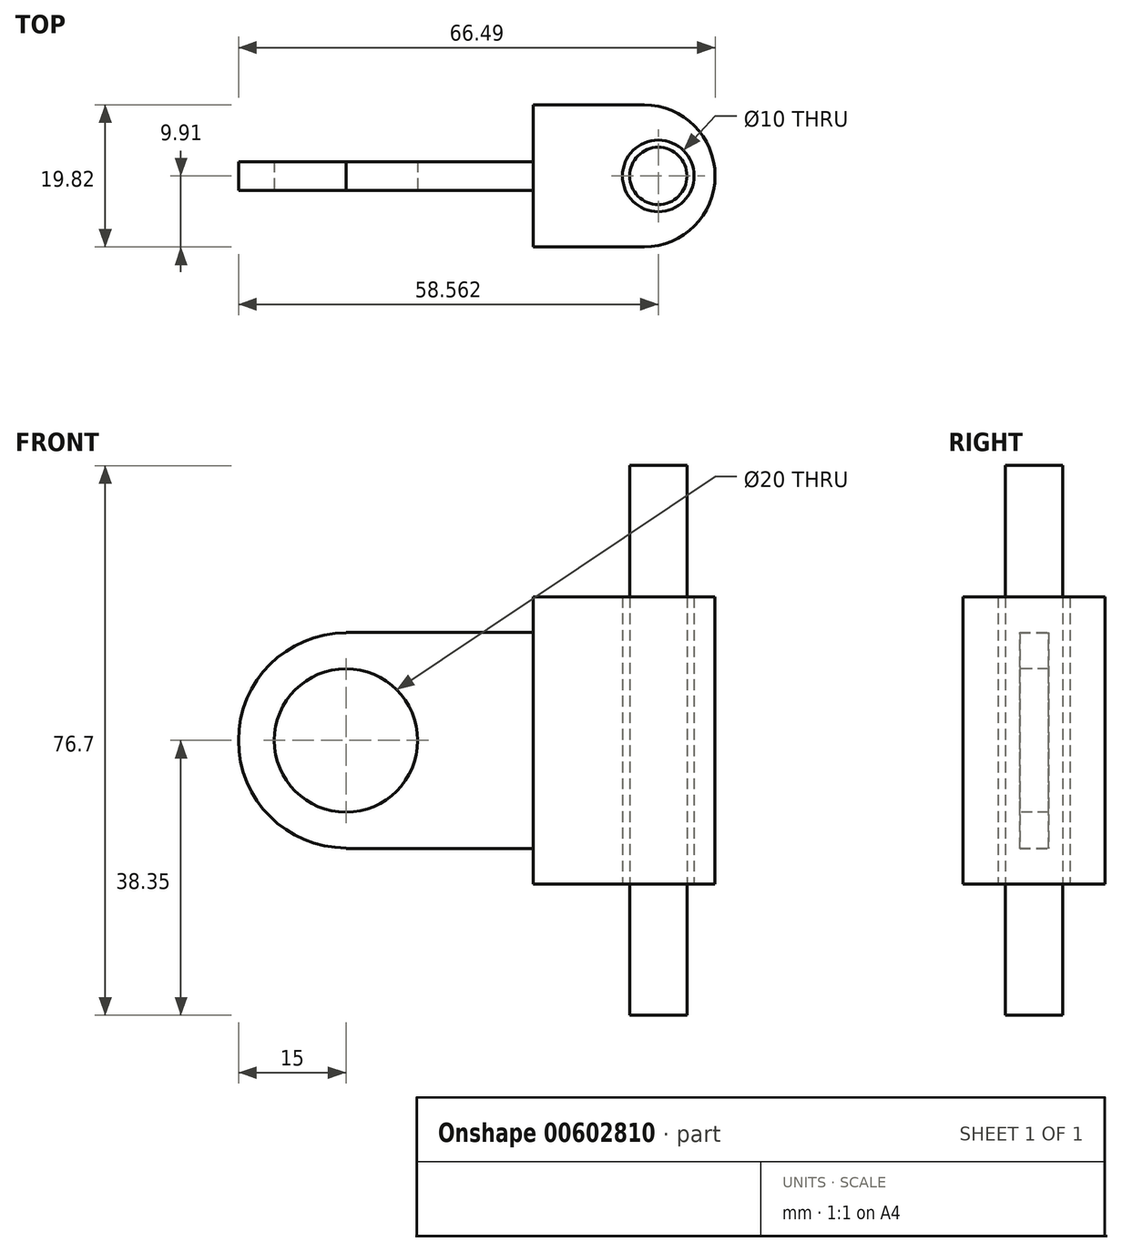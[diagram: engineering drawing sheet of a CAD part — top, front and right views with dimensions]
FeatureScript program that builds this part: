
annotation { "Feature Type Name" : "Feature", "Feature Type Description" : "" }
export const myFeature = defineFeature(function(context is Context, id is Id, definition is map)
    precondition{}
    {
        {
            var Q0;
            Q0=qCreatedBy(makeId("Front.planeOp"),FACE);
            var sketch = newSketch(context, id + "F0", { "sketchPlane" : qUnion([Q0])});
            skCircle(sketch, "E0", {"center": v(0, 0) * mm, "radius": 15 * mm});
            skSolve(sketch);
        }
        {
            var Q0;
            Q0=makeQuery(id+"F0.imprint","IMPRINT",FACE,{"disambiguationData":[TD([[makeQuery(id+"F0.imprint","IMPRINT",EDGE,{"derivedFrom":sQuery(id+"F0.wireOp",EDGE,"E0")}),1.0]])]});
            extrude(context, id + "F1", {"entities" : qUnion([Q0]), "endBound" : BoundingType.SYMMETRIC, "depth" : 4 * mm, "offsetDistance" : 25.4 * mm});
        }
        {
            var Q0;
            Q0=makeQuery(id+"F1.opExtrude","CAP_FACE",FACE,{"disambiguationData":[OSD([sQuery(id+"F0.wireOp",EDGE,"E0")])],"isStart":false});
            var sketch = newSketch(context, id + "F2", { "sketchPlane" : qUnion([Q0])});
            skPoint(sketch, "E1", {"position": v(0, 0) * mm});
            skSolve(sketch);
        }
        {
            var Q0;
            Q0=qCreatedBy(makeId("Front.planeOp"),FACE);
            var sketch = newSketch(context, id + "F3", { "sketchPlane" : qUnion([Q0])});
            skLineSegment(sketch, "E2.bottom", {"start": v(0, 0) * mm, "end": v(26.09, 0) * mm});
            skLineSegment(sketch, "E2.top", {"start": v(0, 15.07) * mm, "end": v(26.09, 15.07) * mm});
            skLineSegment(sketch, "E2.left", {"start": v(0, 0) * mm, "end": v(0, 15.07) * mm});
            skLineSegment(sketch, "E2.right", {"start": v(26.09, 0) * mm, "end": v(26.09, 15.07) * mm});
            skSolve(sketch);
        }
        {
            var Q0;
            Q0=makeQuery(id+"F3.imprint","IMPRINT",FACE,{"disambiguationData":[TD([[makeQuery(id+"F3.imprint","IMPRINT",EDGE,{"derivedFrom":sQuery(id+"F3.wireOp",EDGE,"E2.bottom")}),1.0]])]});
            extrude(context, id + "F4", {"entities" : qUnion([Q0]), "operationType" : NewBodyOperationType.ADD, "endBound" : BoundingType.SYMMETRIC, "depth" : 4 * mm, "offsetDistance" : 25.4 * mm});
        }
        {
            var Q0;
            Q0=makeQuery(id+"F1.opExtrude","SWEPT_BODY",BODY,{"disambiguationData":[OSD([sQuery(id+"F0.wireOp",EDGE,"E0")])]});
            var Q1;
            Q1=qCreatedBy(makeId("Top.planeOp"),FACE);
            mirror(context, id + "F5", {"operationType" : NewBodyOperationType.ADD, "entities" : qUnion([Q0]), "mirrorPlane" : qUnion([Q1])});
        }
        {
            var Q0;
            Q0=sQuery(id+"F2.wireOp",VERTEX,"E1");
            var Q1;
            Q1=makeQuery(id+"F1.opExtrude","SWEPT_BODY",BODY,{"disambiguationData":[OSD([sQuery(id+"F0.wireOp",EDGE,"E0")])]});
            hole(context, id + "F6", {"style" : HoleStyle.SIMPLE, "endStyle" : HoleEndStyle.THROUGH, "holeDiameter" : 20 * mm, "majorDiameter" : 6.35 * mm, "isTappedThrough" : true, "tappedDepth" : 12.7 * mm, "tapClearance" : 3, "locations" : qUnion([Q0]), "scope" : qUnion([Q1])});
        }
        {
            var Q0;
            {var subQ0=makeQuery(id+"F4.opExtrude","SWEPT_FACE",FACE,{"disambiguationData":[OSD([sQuery(id+"F3.wireOp",EDGE,"E2.right")])]});Q0=makeQuery(id+"F5.boolean.opBoolean","MERGE",FACE,{"derivedFrom":[subQ0,makeQuery(id+"F5.opPattern","COPY",FACE,{"derivedFrom":subQ0,"instanceName":"1"})]});}
            var sketch = newSketch(context, id + "F7", { "sketchPlane" : qUnion([Q0])});
            skLineSegment(sketch, "E3.bottom", {"start": v(9.9, -20.02) * mm, "end": v(-9.9, -20.02) * mm});
            skLineSegment(sketch, "E3.top", {"start": v(9.9, 20.02) * mm, "end": v(-9.9, 20.02) * mm});
            skLineSegment(sketch, "E3.left", {"start": v(9.9, -20.02) * mm, "end": v(9.9, 20.02) * mm});
            skLineSegment(sketch, "E3.right", {"start": v(-9.9, -20.02) * mm, "end": v(-9.9, 20.02) * mm});
            skPoint(sketch, "E3.middle", {"position": v(0, 0) * mm});
            skSolve(sketch);
        }
        {
            var Q0;
            Q0=makeQuery(id+"F7.imprint","IMPRINT",FACE,{"disambiguationData":[TD([[makeQuery(id+"F7.imprint","IMPRINT",EDGE,{"derivedFrom":sQuery(id+"F7.wireOp",EDGE,"E3.bottom")}),-1.0]])]});
            var Q1;
            {var subQ0=sQuery(id+"F3.wireOp",EDGE,"E2.right");var subQ1=makeQuery(id+"F4.opExtrude","SWEPT_EDGE",EDGE,{"disambiguationData":[OSD([sQuery(id+"F3.wireOp",EDGE,"E2.top"),subQ0])]});Q1=makeQuery(id+"F7.imprint","IMPRINT",FACE,{"disambiguationData":[TD([[makeQuery(id+"F7.imprint","IMPRINT",EDGE,{"derivedFrom":subQ1}),-1.0]])]});}
            extrude(context, id + "F8", {"entities" : qUnion([Q0, Q1]), "depth" : 25.4 * mm, "offsetDistance" : 25.4 * mm});
        }
        {
            var Q0;
            Q0=makeQuery(id+"F8.opExtrude","CAP_EDGE",EDGE,{"disambiguationData":[OSD([sQuery(id+"F7.wireOp",EDGE,"E3.right")])],"isStart":false});
            var Q1;
            Q1=makeQuery(id+"F8.opExtrude","CAP_EDGE",EDGE,{"disambiguationData":[OSD([sQuery(id+"F7.wireOp",EDGE,"E3.left")])],"isStart":false});
            fillet(context, id + "F9", {"entities" : qUnion([Q0, Q1]), "radius" : 9.9 * mm, "tangentPropagation" : true, "allowEdgeOverflow" : false});
        }
        {
            var Q0;
            Q0=makeQuery(id+"F8.opExtrude","SWEPT_FACE",FACE,{"disambiguationData":[OSD([sQuery(id+"F7.wireOp",EDGE,"E3.bottom")])]});
            var sketch = newSketch(context, id + "F10", { "sketchPlane" : qUnion([Q0])});
            skPoint(sketch, "E4", {"position": v(43.56, 0) * mm});
            skSolve(sketch);
        }
        {
            var Q0;
            Q0=sQuery(id+"F10.wireOp",VERTEX,"E4");
            var Q1;
            Q1=makeQuery(id+"F8.opExtrude","SWEPT_BODY",BODY,{"disambiguationData":[OSD([sQuery(id+"F7.wireOp",EDGE,"E3.bottom"),sQuery(id+"F7.wireOp",EDGE,"E3.top"),sQuery(id+"F7.wireOp",EDGE,"E3.left"),sQuery(id+"F7.wireOp",EDGE,"E3.right")])]});
            hole(context, id + "F11", {"style" : HoleStyle.SIMPLE, "endStyle" : HoleEndStyle.THROUGH, "holeDiameter" : 10 * mm, "majorDiameter" : 6.35 * mm, "isTappedThrough" : true, "tappedDepth" : 12.7 * mm, "tapClearance" : 3, "locations" : qUnion([Q0]), "scope" : qUnion([Q1])});
        }
        {
            var Q0;
            Q0=qCreatedBy(makeId("Top.planeOp"),FACE);
            var sketch = newSketch(context, id + "F12", { "sketchPlane" : qUnion([Q0])});
            skCircle(sketch, "E5", {"center": v(43.57, 0) * mm, "radius": 4 * mm});
            skSolve(sketch);
        }
        {
            var Q0;
            Q0=makeQuery(id+"F12.imprint","IMPRINT",FACE,{"disambiguationData":[TD([[makeQuery(id+"F12.imprint","IMPRINT",EDGE,{"derivedFrom":sQuery(id+"F12.wireOp",EDGE,"E5")}),1.0]])]});
            extrude(context, id + "F13", {"entities" : qUnion([Q0]), "endBound" : BoundingType.SYMMETRIC, "depth" : 76.7 * mm, "offsetDistance" : 25.4 * mm});
        }
    });
